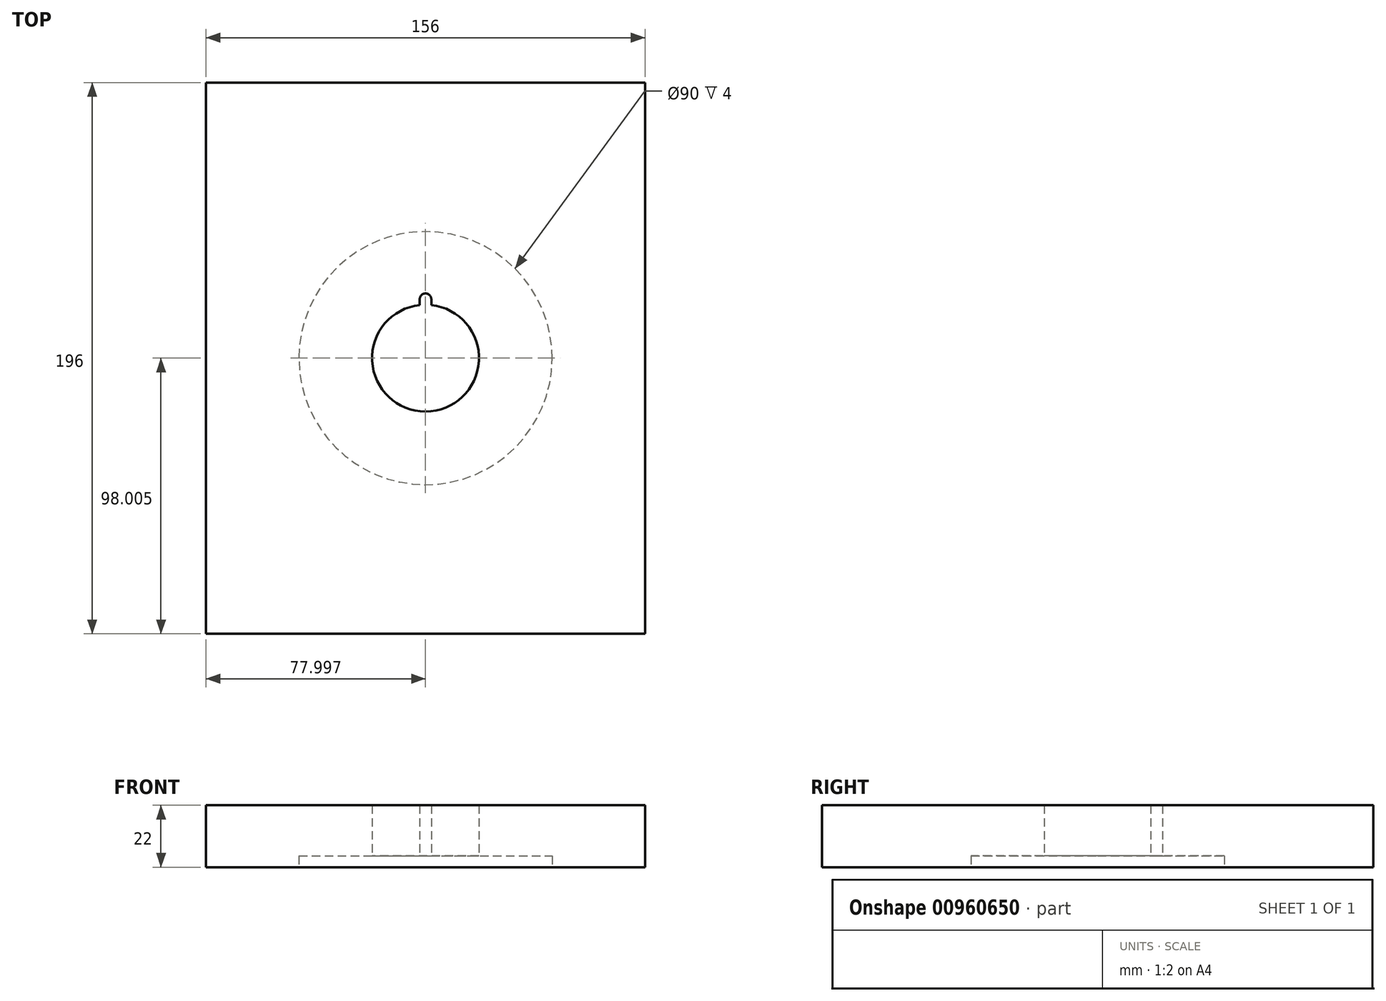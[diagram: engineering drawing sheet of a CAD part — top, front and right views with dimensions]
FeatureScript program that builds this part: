
annotation { "Feature Type Name" : "Feature", "Feature Type Description" : "" }
export const myFeature = defineFeature(function(context is Context, id is Id, definition is map)
    precondition{}
    {
        {
            var Q0;
            Q0=qCreatedBy(makeId("Top.planeOp"),FACE);
            var sketch = newSketch(context, id + "F0", { "sketchPlane" : qUnion([Q0])});
            skLineSegment(sketch, "E0.bottom", {"start": v(-77.08, 118.88) * mm, "end": v(78.92, 118.88) * mm});
            skLineSegment(sketch, "E0.top", {"start": v(-77.08, -77.12) * mm, "end": v(78.92, -77.12) * mm});
            skLineSegment(sketch, "E0.left", {"start": v(-77.08, 118.88) * mm, "end": v(-77.08, -77.12) * mm});
            skLineSegment(sketch, "E0.right", {"start": v(78.92, 118.88) * mm, "end": v(78.92, -77.12) * mm});
            skLineSegment(sketch, "E1", {"start": v(-77.08, 20.88) * mm, "end": v(78.92, 20.88) * mm, "construction": true});
            skArc(sketch, "E2", {"start": v(-1.13, 39.77) * mm, "mid": v(0.92, 1.88) * mm, "end": v(2.97, 39.77) * mm});
            skLineSegment(sketch, "E3", {"start": v(2.97, 39.77) * mm, "end": v(2.97, 41.83) * mm});
            skLineSegment(sketch, "E4.MirrorCS", {"start": v(-1.13, 39.77) * mm, "end": v(-1.13, 41.83) * mm});
            skArc(sketch, "E5", {"start": v(2.97, 41.83) * mm, "mid": v(0.92, 43.88) * mm, "end": v(-1.13, 41.83) * mm});
            skPoint(sketch, "E6.orphan", {"position": v(-1.13, 43.88) * mm});
            skPoint(sketch, "E7.orphan", {"position": v(2.97, 43.88) * mm});
            skPoint(sketch, "E8.orphan", {"position": v(-1.13, 41.83) * mm});
            skPoint(sketch, "E9.start.orphan", {"position": v(0.92, 43.88) * mm});
            skLineSegment(sketch, "E10", {"start": v(0.92, 118.88) * mm, "end": v(0.92, -77.12) * mm, "construction": true});
            skSolve(sketch);
        }
        {
            var Q0;
            Q0=makeQuery(id+"F0.imprint","IMPRINT",FACE,{"disambiguationData":[TD([[makeQuery(id+"F0.imprint","IMPRINT",EDGE,{"derivedFrom":sQuery(id+"F0.wireOp",EDGE,"E0.bottom")}),-1.0]])]});
            var Q1;
            Q1=makeQuery(id+"F0.imprint","IMPRINT",FACE,{"disambiguationData":[TD([[makeQuery(id+"F0.imprint","IMPRINT",EDGE,{"derivedFrom":sQuery(id+"F0.wireOp",EDGE,"E2")}),-1.0]])]});
            extrude(context, id + "F1", {"entities" : qUnion([Q0, Q1]), "depth" : 22 * mm, "offsetDistance" : 25 * mm});
        }
        {
            var Q0;
            Q0=makeQuery(id+"F0.imprint","IMPRINT",FACE,{"disambiguationData":[TD([[makeQuery(id+"F0.imprint","IMPRINT",EDGE,{"derivedFrom":sQuery(id+"F0.wireOp",EDGE,"E2")}),-1.0]])]});
            extrude(context, id + "F2", {"entities" : qUnion([Q0]), "operationType" : NewBodyOperationType.ADD, "depth" : 4 * mm, "offsetDistance" : 25 * mm});
        }
        {
            var Q0;
            Q0=makeQuery(id+"F1.opExtrude","CAP_FACE",FACE,{"disambiguationData":[OSD([sQuery(id+"F0.wireOp",EDGE,"E0.bottom"),sQuery(id+"F0.wireOp",EDGE,"E0.top"),sQuery(id+"F0.wireOp",EDGE,"E0.left"),sQuery(id+"F0.wireOp",EDGE,"E0.right"),sQuery(id+"F0.wireOp",EDGE,"E2"),sQuery(id+"F0.wireOp",EDGE,"E3"),sQuery(id+"F0.wireOp",EDGE,"E4.MirrorCS"),sQuery(id+"F0.wireOp",EDGE,"E5")])],"isStart":true});
            var sketch = newSketch(context, id + "F3", { "sketchPlane" : qUnion([Q0])});
            skCircle(sketch, "E11", {"center": v(0.92, -20.88) * mm, "radius": 45 * mm});
            skSolve(sketch);
        }
        {
            var Q0;
            Q0 = qSketchRegion(id + "F3", true);
            extrude(context, id + "F4", {"entities" : qUnion([Q0]), "operationType" : NewBodyOperationType.REMOVE, "oppositeDirection" : true, "depth" : 4 * mm, "offsetDistance" : 25 * mm});
        }
    });
